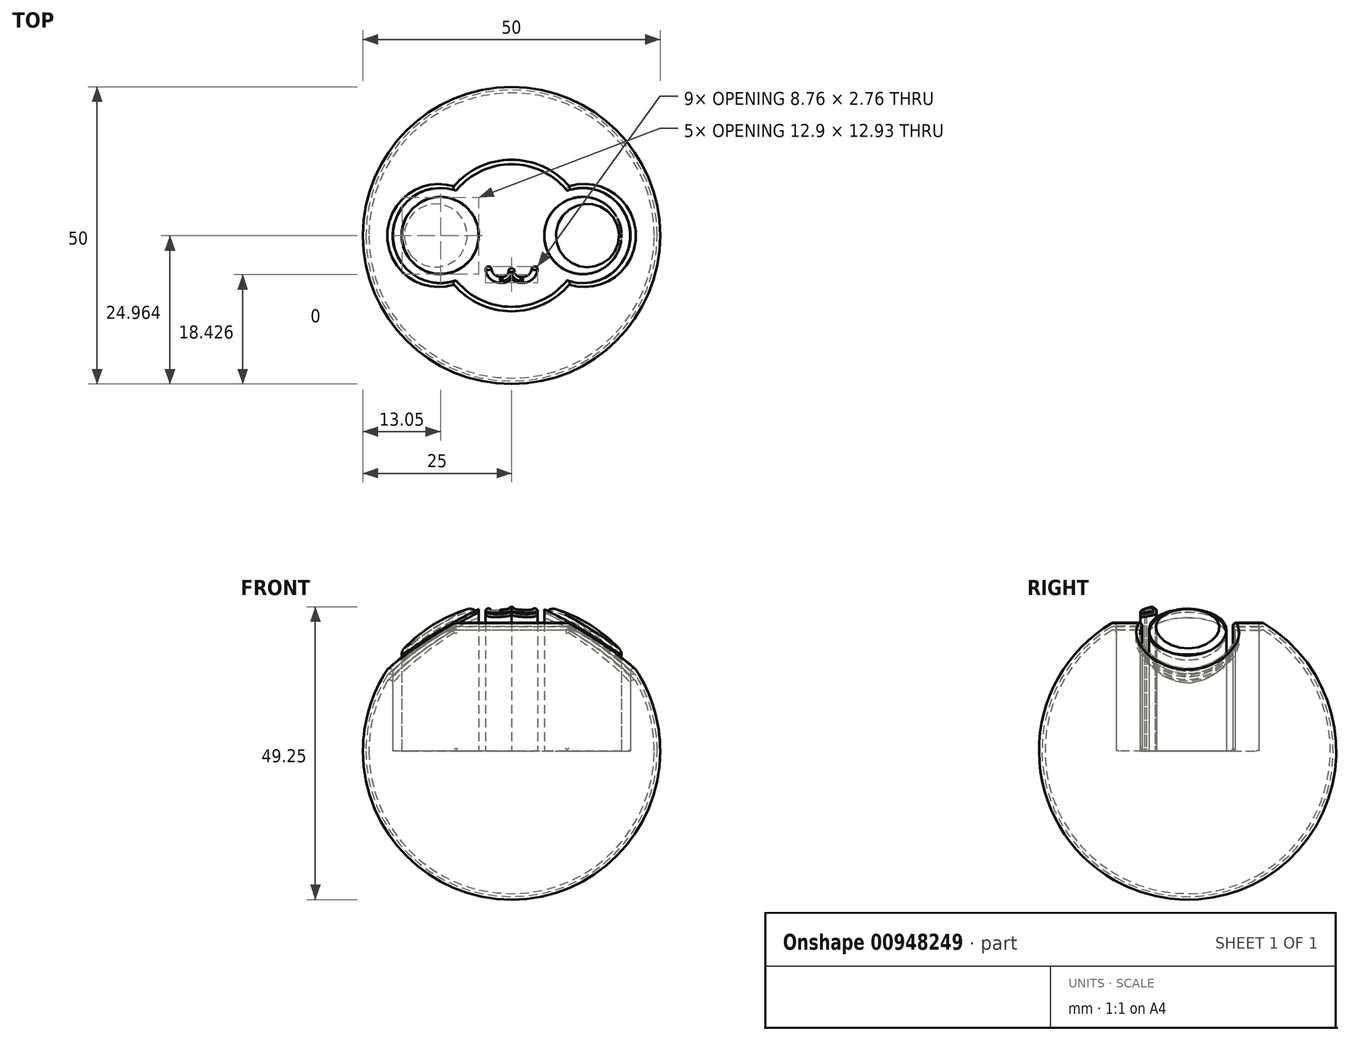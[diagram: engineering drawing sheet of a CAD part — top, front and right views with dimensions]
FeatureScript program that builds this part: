
annotation { "Feature Type Name" : "Feature", "Feature Type Description" : "" }
export const myFeature = defineFeature(function(context is Context, id is Id, definition is map)
    precondition{}
    {
        {
            var Q0;
            Q0=qCreatedBy(makeId("Top.planeOp"),FACE);
            var sketch = newSketch(context, id + "F0", { "sketchPlane" : qUnion([Q0])});
            skCircle(sketch, "E0", {"center": v(0, 0) * mm, "radius": 25 * mm});
            skLineSegment(sketch, "E1", {"start": v(0, 0) * mm, "end": v(25, 0) * mm});
            skLineSegment(sketch, "E2", {"start": v(0, 0) * mm, "end": v(-25, 0) * mm});
            skCircle(sketch, "E3", {"center": v(0, 0) * mm, "radius": 24 * mm});
            skCircle(sketch, "E4", {"center": v(0, 0) * mm, "radius": 24.5 * mm});
            skSolve(sketch);
        }
        {
            var Q0;
            {var subQ0=sQuery(id+"F0.wireOp",EDGE,"E3");var subQ1=sQuery(id+"F0.wireOp",EDGE,"E1");var subQ2=makeQuery(id+"F0.imprint","INTERSECT",VERTEX,{"derivedFrom":[subQ1,subQ0]});Q0=makeQuery(id+"F0.imprint","IMPRINT",FACE,{"disambiguationData":[TD([[makeQuery(id+"F0.imprint","IMPRINT",EDGE,{"disambiguationData":[TD([[subQ2,-1.0]])],"derivedFrom":subQ1}),-1.0]])]});}
            var Q1;
            {var subQ0=sQuery(id+"F0.wireOp",EDGE,"E1");var subQ1=sQuery(id+"F0.wireOp",EDGE,"E0");var subQ2=makeQuery(id+"F0.imprint","INTERSECT",VERTEX,{"derivedFrom":[subQ1,subQ0]});Q1=makeQuery(id+"F0.imprint","IMPRINT",FACE,{"disambiguationData":[TD([[makeQuery(id+"F0.imprint","IMPRINT",EDGE,{"disambiguationData":[TD([[subQ2,1.0]])],"derivedFrom":subQ1}),1.0]])]});}
            var Q2;
            {var subQ0=sQuery(id+"F0.wireOp",EDGE,"E2");var subQ1=sQuery(id+"F0.wireOp",EDGE,"E1");var subQ2=makeQuery(id+"F0.imprint","INTERSECT",VERTEX,{"derivedFrom":[subQ1,subQ0]});Q2=makeQuery(id+"F0.imprint","IMPRINT",FACE,{"disambiguationData":[TD([[makeQuery(id+"F0.imprint","IMPRINT",EDGE,{"disambiguationData":[TD([[subQ2,-1.0]])],"derivedFrom":subQ1}),-1.0]])]});}
            var Q3;
            Q3=sQuery(id+"F0.wireOp",EDGE,"E1");
            revolve(context, id + "F1", {"surfaceOperationType" : NewSurfaceOperationType.NEW, "entities" : qUnion([Q0, Q1, Q2]), "axis" : qUnion([Q3]), "revolveType" : RevolveType.FULL});
        }
        {
            var Q0;
            {var subQ0=sQuery(id+"F0.wireOp",EDGE,"E2");var subQ1=sQuery(id+"F0.wireOp",EDGE,"E1");var subQ2=makeQuery(id+"F0.imprint","INTERSECT",VERTEX,{"derivedFrom":[subQ1,subQ0]});Q0=makeQuery(id+"F0.imprint","IMPRINT",FACE,{"disambiguationData":[TD([[makeQuery(id+"F0.imprint","IMPRINT",EDGE,{"disambiguationData":[TD([[subQ2,-1.0]])],"derivedFrom":subQ1}),-1.0]])]});}
            var Q1;
            {var subQ0=sQuery(id+"F0.wireOp",EDGE,"E3");var subQ1=sQuery(id+"F0.wireOp",EDGE,"E1");var subQ2=makeQuery(id+"F0.imprint","INTERSECT",VERTEX,{"derivedFrom":[subQ1,subQ0]});Q1=makeQuery(id+"F0.imprint","IMPRINT",FACE,{"disambiguationData":[TD([[makeQuery(id+"F0.imprint","IMPRINT",EDGE,{"disambiguationData":[TD([[subQ2,-1.0]])],"derivedFrom":subQ1}),-1.0]])]});}
            var Q2;
            Q2=sQuery(id+"F0.wireOp",EDGE,"E1");
            revolve(context, id + "F2", {"surfaceOperationType" : NewSurfaceOperationType.NEW, "entities" : qUnion([Q0, Q1]), "axis" : qUnion([Q2]), "revolveType" : RevolveType.FULL});
        }
        {
            var Q0;
            {var subQ0=sQuery(id+"F0.wireOp",EDGE,"E2");var subQ1=sQuery(id+"F0.wireOp",EDGE,"E1");var subQ2=makeQuery(id+"F0.imprint","INTERSECT",VERTEX,{"derivedFrom":[subQ1,subQ0]});Q0=makeQuery(id+"F0.imprint","IMPRINT",FACE,{"disambiguationData":[TD([[makeQuery(id+"F0.imprint","IMPRINT",EDGE,{"disambiguationData":[TD([[subQ2,-1.0]])],"derivedFrom":subQ1}),-1.0]])]});}
            var Q1;
            Q1=sQuery(id+"F0.wireOp",EDGE,"E1");
            revolve(context, id + "F3", {"surfaceOperationType" : NewSurfaceOperationType.NEW, "entities" : qUnion([Q0]), "axis" : qUnion([Q1]), "revolveType" : RevolveType.FULL});
        }
        {
            var Q0;
            Q0=qCreatedBy(makeId("Top.planeOp"),FACE);
            var sketch = newSketch(context, id + "F4", { "sketchPlane" : qUnion([Q0])});
            skCircle(sketch, "E5", {"center": v(0, 0) * mm, "radius": 12 * mm});
            skLineSegment(sketch, "E6", {"start": v(0, 0) * mm, "end": v(0, -6) * mm, "construction": true});
            skLineSegment(sketch, "E7", {"start": v(0, -6) * mm, "end": v(0, -6) * mm});
            skLineSegment(sketch, "E8", {"start": v(-1.5, -7.45) * mm, "end": v(-1.9, -7.45) * mm, "construction": true});
            skPoint(sketch, "E9.visualSharp", {"position": v(-4.08, -7.45) * mm});
            skArc(sketch, "E9.filletArc", {"start": v(-3.88, -5.7) * mm, "mid": v(-3.22, -6.95) * mm, "end": v(-1.9, -7.45) * mm, "construction": true});
            skPoint(sketch, "E10.visualSharp", {"position": v(-0.05, -7.45) * mm});
            skArc(sketch, "E10.filletArc", {"start": v(-1.5, -7.45) * mm, "mid": v(-0.46, -7.03) * mm, "end": v(0, -6) * mm, "construction": true});
            skArc(sketch, "E11.MirrorCS", {"start": v(1.5, -7.45) * mm, "mid": v(0.46, -7.03) * mm, "end": v(0, -6) * mm, "construction": true});
            skLineSegment(sketch, "E12.MirrorCS", {"start": v(1.5, -7.45) * mm, "end": v(1.9, -7.45) * mm, "construction": true});
            skArc(sketch, "E13.MirrorCS", {"start": v(3.88, -5.7) * mm, "mid": v(3.22, -6.95) * mm, "end": v(1.9, -7.45) * mm, "construction": true});
            skArc(sketch, "E14.0.startCap", {"start": v(-1.5, -7.95) * mm, "mid": v(-2, -7.45) * mm, "end": v(-1.5, -6.95) * mm, "construction": true});
            skArc(sketch, "E14.0.endCap", {"start": v(-0.5, -5.98) * mm, "mid": v(0.02, -5.5) * mm, "end": v(0.5, -6.02) * mm});
            skArc(sketch, "E14.0.left", {"start": v(-1.5, -6.95) * mm, "mid": v(-0.8, -6.67) * mm, "end": v(-0.5, -5.98) * mm});
            skArc(sketch, "E14.0.right", {"start": v(-1.5, -7.95) * mm, "mid": v(-0.1, -7.39) * mm, "end": v(0.5, -6.02) * mm});
            skArc(sketch, "E14.1.startCap", {"start": v(-1.5, -6.95) * mm, "mid": v(-1, -7.45) * mm, "end": v(-1.5, -7.95) * mm, "construction": true});
            skArc(sketch, "E14.1.endCap", {"start": v(-1.9, -7.95) * mm, "mid": v(-2.4, -7.45) * mm, "end": v(-1.9, -6.95) * mm, "construction": true});
            skLineSegment(sketch, "E14.1.left", {"start": v(-1.5, -7.95) * mm, "end": v(-1.9, -7.95) * mm});
            skLineSegment(sketch, "E14.1.right", {"start": v(-1.5, -6.95) * mm, "end": v(-1.9, -6.95) * mm});
            skArc(sketch, "E14.2.startCap", {"start": v(-4.38, -5.75) * mm, "mid": v(-3.94, -5.2) * mm, "end": v(-3.39, -5.63) * mm});
            skArc(sketch, "E14.2.endCap", {"start": v(-1.9, -6.95) * mm, "mid": v(-1.4, -7.45) * mm, "end": v(-1.9, -7.95) * mm, "construction": true});
            skArc(sketch, "E14.2.left", {"start": v(-3.39, -5.63) * mm, "mid": v(-2.9, -6.57) * mm, "end": v(-1.9, -6.95) * mm});
            skArc(sketch, "E14.2.right", {"start": v(-4.38, -5.75) * mm, "mid": v(-3.56, -7.32) * mm, "end": v(-1.9, -7.95) * mm});
            skArc(sketch, "E15.0.startCap", {"start": v(1.5, -6.95) * mm, "mid": v(2, -7.45) * mm, "end": v(1.5, -7.95) * mm, "construction": true});
            skArc(sketch, "E15.0.endCap", {"start": v(-0.5, -6.02) * mm, "mid": v(-0.02, -5.5) * mm, "end": v(0.5, -5.98) * mm});
            skArc(sketch, "E15.0.left", {"start": v(1.5, -7.95) * mm, "mid": v(0.1, -7.39) * mm, "end": v(-0.5, -6.02) * mm});
            skArc(sketch, "E15.0.right", {"start": v(1.5, -6.95) * mm, "mid": v(0.8, -6.67) * mm, "end": v(0.5, -5.98) * mm});
            skArc(sketch, "E15.1.startCap", {"start": v(1.5, -7.95) * mm, "mid": v(1, -7.45) * mm, "end": v(1.5, -6.95) * mm, "construction": true});
            skArc(sketch, "E15.1.endCap", {"start": v(1.9, -6.95) * mm, "mid": v(2.4, -7.45) * mm, "end": v(1.9, -7.95) * mm, "construction": true});
            skLineSegment(sketch, "E15.1.left", {"start": v(1.5, -6.95) * mm, "end": v(1.9, -6.95) * mm});
            skLineSegment(sketch, "E15.1.right", {"start": v(1.5, -7.95) * mm, "end": v(1.9, -7.95) * mm});
            skArc(sketch, "E15.2.startCap", {"start": v(3.39, -5.63) * mm, "mid": v(3.94, -5.2) * mm, "end": v(4.38, -5.75) * mm});
            skArc(sketch, "E15.2.endCap", {"start": v(1.9, -7.95) * mm, "mid": v(1.4, -7.45) * mm, "end": v(1.9, -6.95) * mm, "construction": true});
            skArc(sketch, "E15.2.left", {"start": v(4.38, -5.75) * mm, "mid": v(3.56, -7.32) * mm, "end": v(1.9, -7.95) * mm});
            skArc(sketch, "E15.2.right", {"start": v(3.39, -5.63) * mm, "mid": v(2.9, -6.57) * mm, "end": v(1.9, -6.95) * mm});
            skCircle(sketch, "E16", {"center": v(-12, 0) * mm, "radius": 8 * mm});
            skCircle(sketch, "E17.0", {"center": v(-12, 0) * mm, "radius": 6.5 * mm});
            skCircle(sketch, "E18.MirrorC", {"center": v(12, 0) * mm, "radius": 8 * mm});
            skCircle(sketch, "E19.MirrorC", {"center": v(12, 0) * mm, "radius": 6.5 * mm});
            skLineSegment(sketch, "E20", {"start": v(0, -6) * mm, "end": v(0, -12) * mm, "construction": true});
            skSolve(sketch);
        }
        {
            var Q0;
            {var subQ2=sQuery(id+"F4.wireOp",EDGE,"E14.0.left");Q0=makeQuery(id+"F4.imprint","IMPRINT",FACE,{"disambiguationData":[TD([[makeQuery(id+"F4.imprint","IMPRINT",EDGE,{"derivedFrom":subQ2}),1.0]])]});}
            var Q1;
            {var subQ0=sQuery(id+"F4.wireOp",EDGE,"E16");var subQ1=sQuery(id+"F4.wireOp",EDGE,"E5");var subQ2=makeQuery(id+"F4.imprint","INTERSECT",VERTEX,{"disambiguationData":[OD(0.0)],"derivedFrom":[subQ1,subQ0]});Q1=makeQuery(id+"F4.imprint","IMPRINT",FACE,{"disambiguationData":[TD([[makeQuery(id+"F4.imprint","IMPRINT",EDGE,{"disambiguationData":[TD([[subQ2,-1.0]])],"derivedFrom":subQ1}),-1.0]])]});}
            var Q2;
            {var subQ0=sQuery(id+"F4.wireOp",EDGE,"E16");var subQ1=sQuery(id+"F4.wireOp",EDGE,"E5");var subQ2=makeQuery(id+"F4.imprint","INTERSECT",VERTEX,{"disambiguationData":[OD(0.0)],"derivedFrom":[subQ1,subQ0]});Q2=makeQuery(id+"F4.imprint","IMPRINT",FACE,{"disambiguationData":[TD([[makeQuery(id+"F4.imprint","IMPRINT",EDGE,{"disambiguationData":[TD([[subQ2,-1.0]])],"derivedFrom":subQ1}),1.0]])]});}
            var Q3;
            {var subQ0=sQuery(id+"F4.wireOp",EDGE,"E18.MirrorC");var subQ1=sQuery(id+"F4.wireOp",EDGE,"E5");var subQ2=makeQuery(id+"F4.imprint","INTERSECT",VERTEX,{"disambiguationData":[OD(0.0)],"derivedFrom":[subQ1,subQ0]});Q3=makeQuery(id+"F4.imprint","IMPRINT",FACE,{"disambiguationData":[TD([[makeQuery(id+"F4.imprint","IMPRINT",EDGE,{"disambiguationData":[TD([[subQ2,1.0]])],"derivedFrom":subQ1}),1.0]])]});}
            var Q4;
            {var subQ0=sQuery(id+"F4.wireOp",EDGE,"E18.MirrorC");var subQ1=sQuery(id+"F4.wireOp",EDGE,"E5");var subQ2=makeQuery(id+"F4.imprint","INTERSECT",VERTEX,{"disambiguationData":[OD(0.0)],"derivedFrom":[subQ1,subQ0]});Q4=makeQuery(id+"F4.imprint","IMPRINT",FACE,{"disambiguationData":[TD([[makeQuery(id+"F4.imprint","IMPRINT",EDGE,{"disambiguationData":[TD([[subQ2,1.0]])],"derivedFrom":subQ1}),-1.0]])]});}
            extrude(context, id + "F5", {"entities" : qUnion([Q0, Q1, Q2, Q3, Q4]), "operationType" : NewBodyOperationType.REMOVE, "depth" : 31 * mm, "offsetDistance" : 25 * mm});
        }
        {
            var Q0;
            Q0=makeQuery(id+"F5.boolean.opBoolean","SPLIT",FACE,{"disambiguationData":[TD([makeQuery(id+"F5.opExtrude","SWEPT_FACE",FACE,{"disambiguationData":[OSD([sQuery(id+"F4.wireOp",EDGE,"E17.0")])]})])],"derivedFrom":makeQuery(id+"F1.opRevolve","SWEPT_FACE",FACE,{"disambiguationData":[OSD([sQuery(id+"F0.wireOp",EDGE,"E0")])]})});
            var Q1;
            Q1=makeQuery(id+"F5.boolean.opBoolean","SPLIT",FACE,{"disambiguationData":[TD([makeQuery(id+"F5.opExtrude","SWEPT_FACE",FACE,{"disambiguationData":[OSD([sQuery(id+"F4.wireOp",EDGE,"E19.MirrorC")])]})])],"derivedFrom":makeQuery(id+"F1.opRevolve","SWEPT_FACE",FACE,{"disambiguationData":[OSD([sQuery(id+"F0.wireOp",EDGE,"E0")])]})});
            fillet(context, id + "F6", {"entities" : qUnion([Q0, Q1]), "radius" : 1.5 * mm, "tangentPropagation" : true, "allowEdgeOverflow" : false});
        }
        {
            var Q0;
            Q0=makeQuery(id+"F5.boolean.opBoolean","COPY",FACE,{"derivedFrom":makeQuery(id+"F5.opExtrude","SWEPT_FACE",FACE,{"disambiguationData":[OSD([sQuery(id+"F4.wireOp",EDGE,"E16")])]})});
            var Q1;
            {var subQ0=sQuery(id+"F4.wireOp",EDGE,"E5");Q1=makeQuery(id+"F5.boolean.opBoolean","COPY",FACE,{"derivedFrom":makeQuery(id+"F5.opExtrude","SWEPT_FACE",FACE,{"disambiguationData":[OSD([subQ0]),TDD([makeQuery(id+"F4.imprint","IMPRINT",EDGE,{"disambiguationData":[TD([[makeQuery(id+"F4.imprint","INTERSECT",VERTEX,{"disambiguationData":[OD(0.0)],"derivedFrom":[subQ0,sQuery(id+"F4.wireOp",EDGE,"E18.MirrorC")]}),-1.0]])],"derivedFrom":subQ0})])]})});}
            var Q2;
            Q2=makeQuery(id+"F5.boolean.opBoolean","COPY",FACE,{"derivedFrom":makeQuery(id+"F5.opExtrude","SWEPT_FACE",FACE,{"disambiguationData":[OSD([sQuery(id+"F4.wireOp",EDGE,"E18.MirrorC")])]})});
            var Q3;
            {var subQ0=sQuery(id+"F4.wireOp",EDGE,"E5");Q3=makeQuery(id+"F5.boolean.opBoolean","COPY",FACE,{"derivedFrom":makeQuery(id+"F5.opExtrude","SWEPT_FACE",FACE,{"disambiguationData":[OSD([subQ0]),TDD([makeQuery(id+"F4.imprint","IMPRINT",EDGE,{"disambiguationData":[TD([[makeQuery(id+"F4.imprint","INTERSECT",VERTEX,{"disambiguationData":[OD(1.0)],"derivedFrom":[subQ0,sQuery(id+"F4.wireOp",EDGE,"E16")]}),-1.0]])],"derivedFrom":subQ0})])]})});}
            fillet(context, id + "F7", {"entities" : qUnion([Q0, Q1, Q2, Q3]), "radius" : .5 * mm, "tangentPropagation" : true, "allowEdgeOverflow" : false});
        }
        {
            var Q0;
            Q0=makeQuery(id+"F5.boolean.opBoolean","SPLIT",FACE,{"disambiguationData":[TD([makeQuery(id+"F5.opExtrude","SWEPT_FACE",FACE,{"disambiguationData":[OSD([sQuery(id+"F4.wireOp",EDGE,"E14.0.left")])]})])],"derivedFrom":makeQuery(id+"F1.opRevolve","SWEPT_FACE",FACE,{"disambiguationData":[OSD([sQuery(id+"F0.wireOp",EDGE,"E0")])]})});
            fillet(context, id + "F8", {"entities" : qUnion([Q0]), "radius" : .5 * mm, "tangentPropagation" : true, "allowEdgeOverflow" : false});
        }
    });
